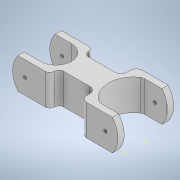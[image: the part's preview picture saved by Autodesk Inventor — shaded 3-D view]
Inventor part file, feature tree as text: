
AUTODESK INVENTOR PART (.ipt)
format: ipt  version: 2022 (Build 260153000, 153)  size: 205,824 bytes
history: native  units: mm
features: fillet x6, sketch x6, extrude x4
ambient origin geometry x8: Origin, YZ Plane, XZ Plane, XY Plane, X Axis, Y Axis, Z Axis, Center Point
bodies: Solid1 (feature_tree)
feature tree (16):
  extrude  "Extrusion1"  Depth=50.0mm TaperAngle=0.0deg
  extrude  "Extrusion2"  Depth=10.0mm
  fillet  "Fillet1"  Radius=20.0mm
  fillet  "Fillet2"  Radius=10.0mm
  fillet  "Fillet3"  Radius=10.0mm
  fillet  "Fillet4"  Radius=10.0mm
  fillet  "Fillet5"  Radius=10.0mm
  fillet  "Fillet6"  Radius=20.0mm
  extrude  "Extrusion3"  Depth=10.0mm
  extrude  "Extrusion4"  Depth=10.0mm
  sketch  "Sketch5"  dims[d34=10.0mm]
  sketch  "Sketch6"  dims[d35=10.0mm d36=10.0mm d37=7.5mm d38=7.5mm d41=200.0mm d42=0.0mm d44=5.0mm d46=5.0mm d47=200.0mm d48=0.0mm]
  sketch  "Sketch1"  dims[d0=100.0mm d3=50.0mm d4=0.0mm]
  sketch  "Sketch2"  dims[d5=60.0mm d13=20.0mm d14=20.0mm d18=10.0mm d19=10.0mm d25=10.0mm d26=10.0mm d27=20.0mm]
  sketch  "Sketch3"  dims[d28=10.0mm d29=10.0mm]
  sketch  "Sketch4"  dims[d31=50.0mm d32=0.0mm d33=10.0mm]
